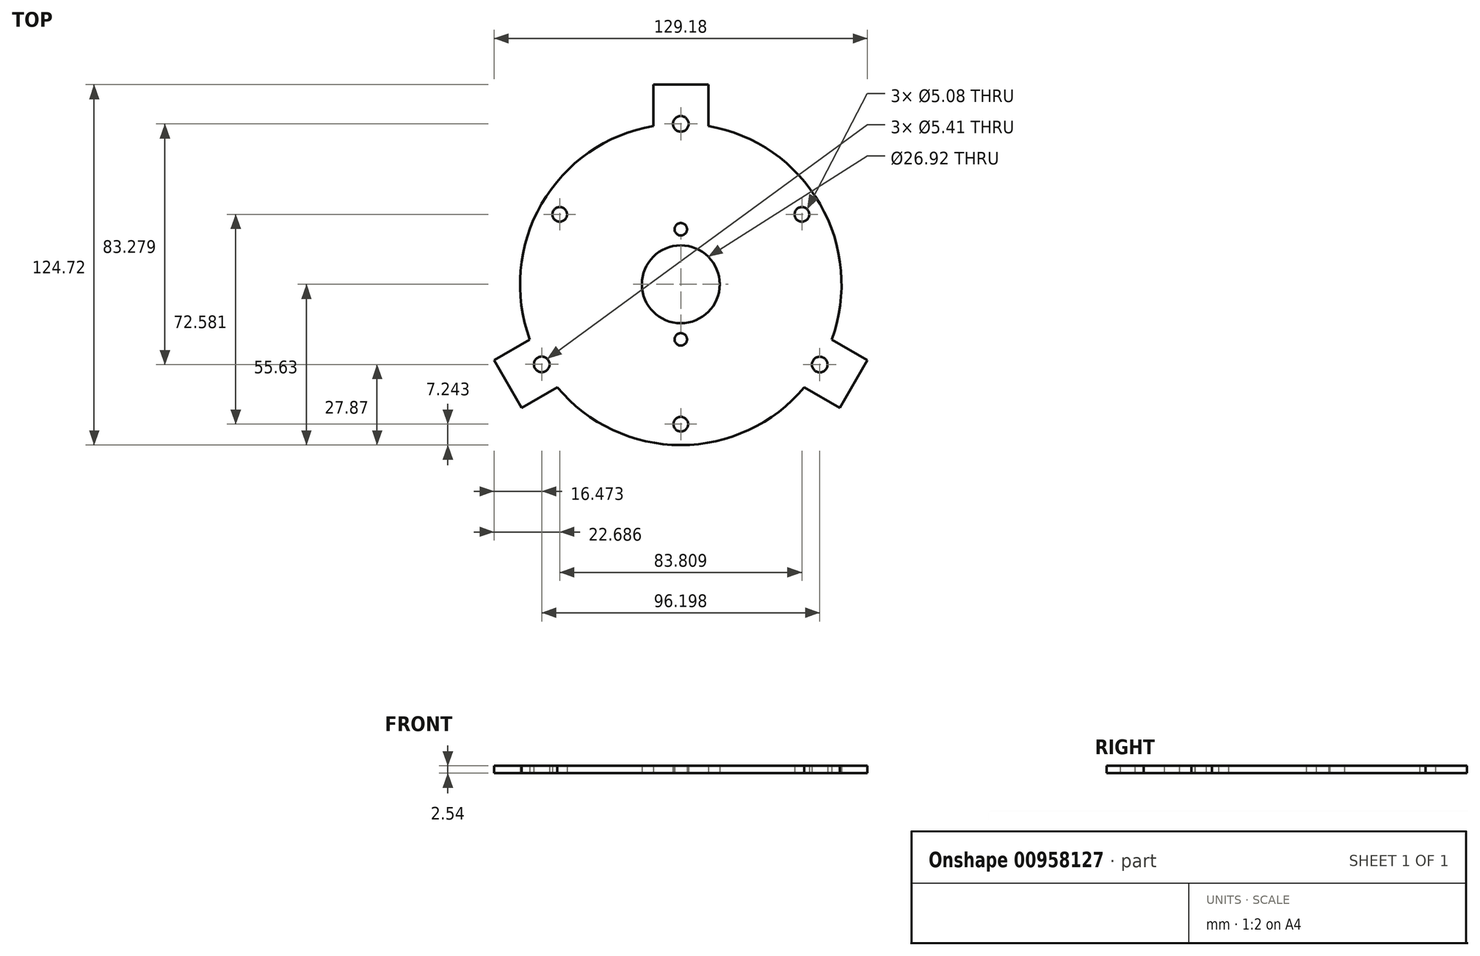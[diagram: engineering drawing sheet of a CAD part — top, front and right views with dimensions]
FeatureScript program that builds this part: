
annotation { "Feature Type Name" : "Feature", "Feature Type Description" : "" }
export const myFeature = defineFeature(function(context is Context, id is Id, definition is map)
    precondition{}
    {
        {
            var Q0;
            Q0=qCreatedBy(makeId("Top.planeOp"),FACE);
            var sketch = newSketch(context, id + "F0", { "sketchPlane" : qUnion([Q0])});
            skArc(sketch, "E0", {"start": v(-9.53, 54.8) * mm, "mid": v(-48.17, 27.81) * mm, "end": v(-52.22, -19.15) * mm});
            skCircle(sketch, "E1", {"center": v(0, 0) * mm, "radius": 13.46 * mm});
            skLineSegment(sketch, "E2", {"start": v(0, 0) * mm, "end": v(0, 13.46) * mm});
            skLineSegment(sketch, "E3", {"start": v(0, 13.46) * mm, "end": v(0, 0) * mm});
            skLineSegment(sketch, "E4", {"start": v(-9.52, 69.09) * mm, "end": v(9.53, 69.09) * mm});
            skLineSegment(sketch, "E5", {"start": v(9.52, 69.09) * mm, "end": v(9.52, 54.8) * mm});
            skLineSegment(sketch, "E6", {"start": v(64.6, -26.3) * mm, "end": v(55.07, -42.8) * mm});
            skLineSegment(sketch, "E7", {"start": v(55.07, -42.8) * mm, "end": v(42.7, -35.65) * mm});
            skLineSegment(sketch, "E8", {"start": v(52.22, -19.15) * mm, "end": v(64.6, -26.3) * mm});
            skLineSegment(sketch, "E9", {"start": v(-64.6, -26.3) * mm, "end": v(-55.07, -42.8) * mm});
            skLineSegment(sketch, "E10", {"start": v(-55.07, -42.8) * mm, "end": v(-42.7, -35.65) * mm});
            skLineSegment(sketch, "E11", {"start": v(-52.22, -19.15) * mm, "end": v(-64.6, -26.3) * mm});
            skLineSegment(sketch, "E12", {"start": v(-9.53, 69.09) * mm, "end": v(-9.53, 54.8) * mm});
            skArc(sketch, "E13.trimOffspring", {"start": v(-42.7, -35.65) * mm, "mid": v(0, -55.63) * mm, "end": v(42.7, -35.65) * mm});
            skArc(sketch, "E14.trimOffspring", {"start": v(52.22, -19.15) * mm, "mid": v(48.17, 27.81) * mm, "end": v(9.53, 54.8) * mm});
            skPoint(sketch, "E15.orphan", {"position": v(-59.83, -34.54) * mm});
            skPoint(sketch, "E16.orphan", {"position": v(59.83, -34.54) * mm});
            skPoint(sketch, "E17.orphan", {"position": v(0, 69.09) * mm});
            skSolve(sketch);
        }
        {
            var Q0;
            Q0 = qSketchRegion(id + "F0", true);
            extrude(context, id + "F1", {"entities" : qUnion([Q0]), "depth" : 2.54 * mm, "offsetDistance" : 25.4 * mm});
        }
        {
            var Q0;
            Q0=qCreatedBy(makeId("Top.planeOp"),FACE);
            var sketch = newSketch(context, id + "F2", { "sketchPlane" : qUnion([Q0])});
            skCircle(sketch, "E18", {"center": v(0, 19.05) * mm, "radius": 2.16 * mm});
            skCircle(sketch, "E19", {"center": v(0, -19.05) * mm, "radius": 2.16 * mm});
            skSolve(sketch);
        }
        {
            var Q0;
            Q0=qCreatedBy(makeId("Top.planeOp"),FACE);
            var sketch = newSketch(context, id + "F3", { "sketchPlane" : qUnion([Q0])});
            skCircle(sketch, "E20", {"center": v(0, 55.52) * mm, "radius": 2.7 * mm});
            skCircle(sketch, "E21", {"center": v(-48.12, -27.7) * mm, "radius": 2.7 * mm});
            skCircle(sketch, "E22", {"center": v(48.08, -27.76) * mm, "radius": 2.7 * mm});
            skPoint(sketch, "E23.orphan", {"position": v(-59.85, -34.55) * mm});
            skPoint(sketch, "E24.orphan", {"position": v(59.85, -34.55) * mm});
            skSolve(sketch);
        }
        {
            var Q0;
            Q0=qCreatedBy(makeId("Top.planeOp"),FACE);
            var sketch = newSketch(context, id + "F4", { "sketchPlane" : qUnion([Q0])});
            skCircle(sketch, "E25", {"center": v(-41.9, 24.2) * mm, "radius": 2.54 * mm});
            skCircle(sketch, "E26", {"center": v(41.9, 24.2) * mm, "radius": 2.54 * mm});
            skCircle(sketch, "E27", {"center": v(0, -48.39) * mm, "radius": 2.54 * mm});
            skSolve(sketch);
        }
        {
            var Q0;
            Q0 = qSketchRegion(id + "F2", true);
            var Q1;
            Q1 = qSketchRegion(id + "F3", true);
            var Q2;
            Q2 = qSketchRegion(id + "F4", true);
            extrude(context, id + "F5", {"entities" : qUnion([Q0, Q1, Q2]), "operationType" : NewBodyOperationType.REMOVE, "depth" : 2.54 * mm, "offsetDistance" : 25.4 * mm});
        }
    });
